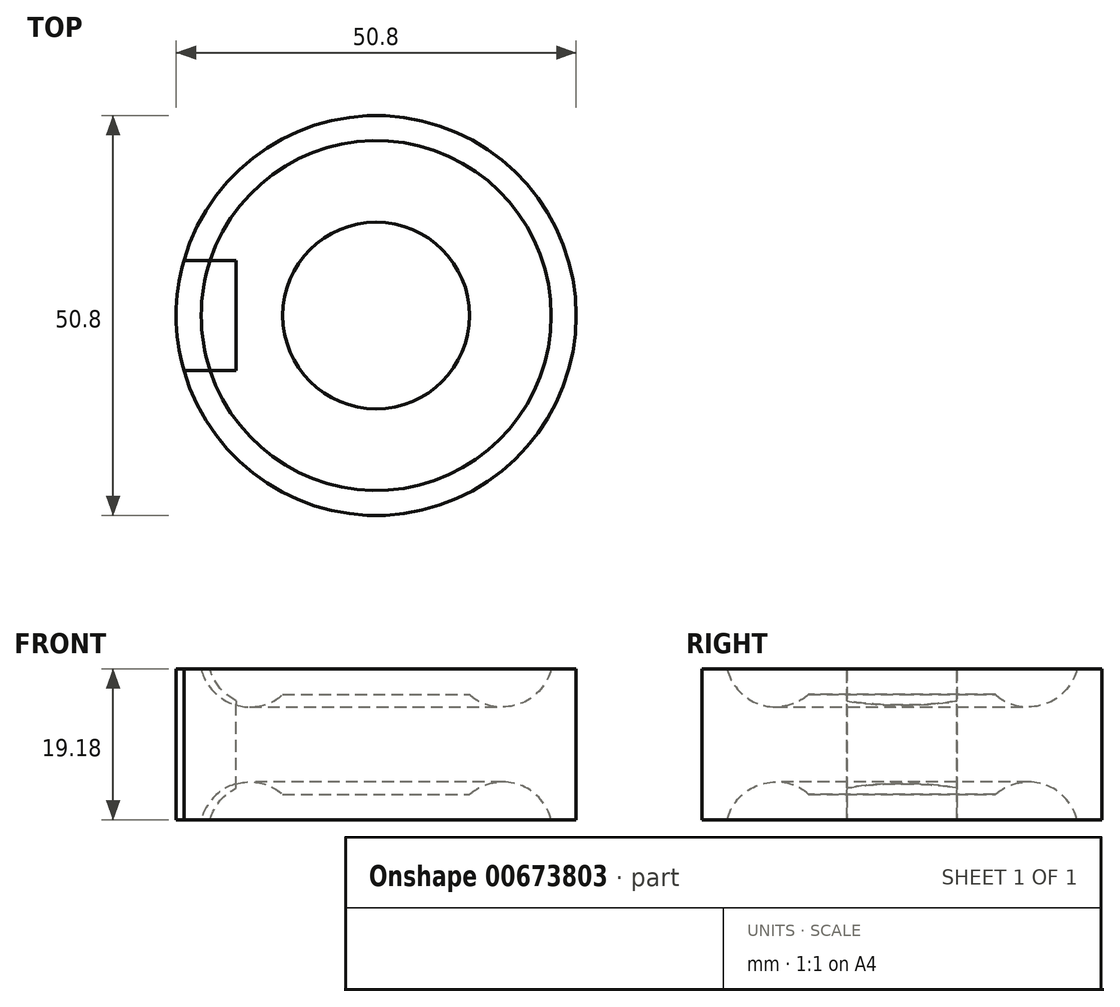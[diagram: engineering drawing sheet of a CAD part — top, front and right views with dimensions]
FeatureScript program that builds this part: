
annotation { "Feature Type Name" : "Feature", "Feature Type Description" : "" }
export const myFeature = defineFeature(function(context is Context, id is Id, definition is map)
    precondition{}
    {
        {
            var Q0;
            Q0=qCreatedBy(makeId("Front.planeOp"),FACE);
            var sketch = newSketch(context, id + "F0", { "sketchPlane" : qUnion([Q0])});
            skLineSegment(sketch, "E0", {"start": v(0, 0) * mm, "end": v(-25.4, 0) * mm});
            skLineSegment(sketch, "E1", {"start": v(-25.4, 0) * mm, "end": v(-25.4, 9.59) * mm});
            skLineSegment(sketch, "E2", {"start": v(-25.4, 9.59) * mm, "end": v(-22.23, 9.59) * mm});
            skArc(sketch, "E3", {"start": v(-22.23, 9.59) * mm, "mid": v(-17.95, 5.05) * mm, "end": v(-11.86, 6.35) * mm});
            skLineSegment(sketch, "E4", {"start": v(0, 0) * mm, "end": v(0, 6.35) * mm});
            skLineSegment(sketch, "E5", {"start": v(0, 6.35) * mm, "end": v(-11.86, 6.35) * mm});
            skSolve(sketch);
        }
        {
            var Q0;
            Q0=makeQuery(id+"F0.imprint","IMPRINT",FACE,{"disambiguationData":[TD([[makeQuery(id+"F0.imprint","IMPRINT",EDGE,{"derivedFrom":sQuery(id+"F0.wireOp",EDGE,"E0")}),-1.0]])]});
            var Q1;
            Q1=sQuery(id+"F0.wireOp",EDGE,"E4");
            revolve(context, id + "F1", {"entities" : qUnion([Q0]), "axis" : qUnion([Q1]), "revolveType" : RevolveType.FULL});
        }
        {
            var Q0;
            Q0=makeQuery(id+"F1.opRevolve","SWEPT_BODY",BODY,{"disambiguationData":[OSD([sQuery(id+"F0.wireOp",EDGE,"E0"),sQuery(id+"F0.wireOp",EDGE,"E1"),sQuery(id+"F0.wireOp",EDGE,"E2"),sQuery(id+"F0.wireOp",EDGE,"E3"),sQuery(id+"F0.wireOp",EDGE,"E4"),sQuery(id+"F0.wireOp",EDGE,"E5")])]});
            var Q1;
            Q1=qCreatedBy(makeId("Top.planeOp"),FACE);
            mirror(context, id + "F2", {"operationType" : NewBodyOperationType.ADD, "entities" : qUnion([Q0]), "mirrorPlane" : qUnion([Q1])});
        }
        {
            var Q0;
            Q0=makeQuery(id+"F1.opRevolve","SWEPT_FACE",FACE,{"disambiguationData":[OSD([sQuery(id+"F0.wireOp",EDGE,"E2")])]});
            var sketch = newSketch(context, id + "F3", { "sketchPlane" : qUnion([Q0])});
            skLineSegment(sketch, "E6.bottom", {"start": v(-30.48, 6.99) * mm, "end": v(-17.78, 6.99) * mm});
            skLineSegment(sketch, "E6.top", {"start": v(-30.48, -6.99) * mm, "end": v(-17.78, -6.99) * mm});
            skLineSegment(sketch, "E6.left", {"start": v(-30.48, 6.99) * mm, "end": v(-30.48, -6.99) * mm});
            skLineSegment(sketch, "E6.right", {"start": v(-17.78, 6.98) * mm, "end": v(-17.78, -6.98) * mm});
            skLineSegment(sketch, "E7", {"start": v(-17.78, 0) * mm, "end": v(0, 0) * mm, "construction": true});
            skSolve(sketch);
        }
        {
            var Q0;
            Q0 = qSketchRegion(id + "F3", true);
            var Q1;
            Q1=makeQuery(id+"F2.opPattern","COPY",FACE,{"derivedFrom":makeQuery(id+"F1.opRevolve","SWEPT_FACE",FACE,{"disambiguationData":[OSD([sQuery(id+"F0.wireOp",EDGE,"E2")])]}),"instanceName":"1"});
            extrude(context, id + "F4", {"entities" : qUnion([Q0]), "endBound" : BoundingType.UP_TO_SURFACE, "oppositeDirection" : true, "depth" : 25.4 * mm, "endBoundEntityFace" : qUnion([Q1]), "offsetDistance" : 25.4 * mm});
        }
        {
            var Q0;
            Q0=makeQuery(id+"F4.opExtrude","SWEPT_BODY",BODY,{"disambiguationData":[OSD([sQuery(id+"F3.wireOp",EDGE,"E6.bottom"),sQuery(id+"F3.wireOp",EDGE,"E6.top"),sQuery(id+"F3.wireOp",EDGE,"E6.left"),sQuery(id+"F3.wireOp",EDGE,"E6.right")])]});
            var Q1;
            Q1=makeQuery(id+"F1.opRevolve","SWEPT_BODY",BODY,{"disambiguationData":[OSD([sQuery(id+"F0.wireOp",EDGE,"E0"),sQuery(id+"F0.wireOp",EDGE,"E1"),sQuery(id+"F0.wireOp",EDGE,"E2"),sQuery(id+"F0.wireOp",EDGE,"E3"),sQuery(id+"F0.wireOp",EDGE,"E4"),sQuery(id+"F0.wireOp",EDGE,"E5")])]});
            booleanBodies(context, id + "F5", {"operationType" : BooleanOperationType.INTERSECTION, "tools" : qUnion([Q0, Q1]), "keepTools" : true});
        }
        {
            var Q0;
            Q0=makeQuery(id+"F4.opExtrude","SWEPT_BODY",BODY,{"disambiguationData":[OSD([sQuery(id+"F3.wireOp",EDGE,"E6.bottom"),sQuery(id+"F3.wireOp",EDGE,"E6.top"),sQuery(id+"F3.wireOp",EDGE,"E6.left"),sQuery(id+"F3.wireOp",EDGE,"E6.right")])]});
            var Q1;
            Q1=makeQuery(id+"F1.opRevolve","SWEPT_BODY",BODY,{"disambiguationData":[OSD([sQuery(id+"F0.wireOp",EDGE,"E0"),sQuery(id+"F0.wireOp",EDGE,"E1"),sQuery(id+"F0.wireOp",EDGE,"E2"),sQuery(id+"F0.wireOp",EDGE,"E3"),sQuery(id+"F0.wireOp",EDGE,"E4"),sQuery(id+"F0.wireOp",EDGE,"E5")])]});
            booleanBodies(context, id + "F6", {"operationType" : BooleanOperationType.SUBTRACTION, "tools" : qUnion([Q0]), "targets" : qUnion([Q1])});
        }
    });
